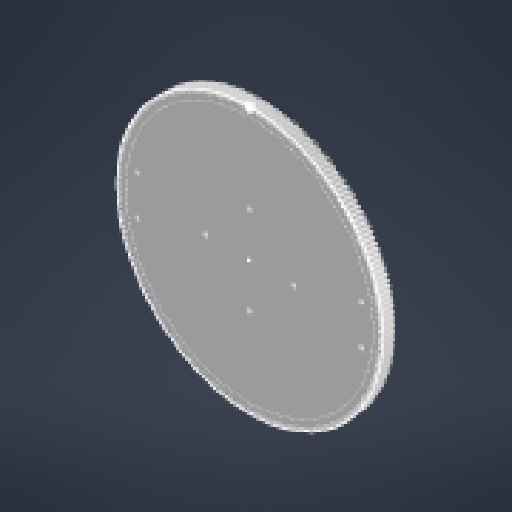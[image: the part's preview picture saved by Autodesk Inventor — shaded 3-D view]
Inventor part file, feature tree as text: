
AUTODESK INVENTOR PART (.ipt)
format: ipt  version: 2023.2 (Build 272271000, 271)  size: 873,472 bytes
history: native  units: mm
features: extrude x7, sketch x6, pattern_circular x1, other x1
ambient origin geometry x8: Origin, YZ Plane, XZ Plane, XY Plane, X Axis, Y Axis, Z Axis, Center Point
bodies: Solid1 (feature_tree)
feature tree (15):
  sketch  "Sketch1"  dims[d0=10.0mm d1=0.0mm]
  extrude  "Extrusion1"  TaperAngle=0.0deg  [1 undecoded]
  extrude  "Extrusion2"  Depth=10.0mm TaperAngle=360.0deg
  pattern_circular  "Circular Pattern1"  [2 undecoded]
  extrude  "Extrusion14"  Depth=10.0mm TaperAngle=0.0deg
  extrude  "Extrusion15"  Depth=10.0mm
  extrude  "Extrusion23"  Depth=10.0mm
  extrude  "Extrusion24"  Depth=10.0mm TaperAngle=0.0deg
  sketch  "Sketch20"  dims[d2=10.0mm d3=0.0mm d4=2000.0mm d5=360.0deg]
  sketch  "Sketch21"  dims[d80=4.0mm]
  sketch  "Sketch29"  dims[d81=4.0mm]
  sketch  "Sketch30"  dims[d82=10.0mm d83=0.0mm]
  sketch  "Sketch31"  dims[d84=4.0mm d85=4.0mm d86=10.0mm d87=0.0mm d116=4.0mm d120=4.0mm d122=10.0mm d123=0.0mm d124=4.0mm d125=4.0mm d126=10.0mm d127=10.0mm d128=10.0mm d129=10.0mm d130=10.0mm d134=10.0mm d135=10.0mm d136=10.0mm d137=10.0mm d138=10.0mm d139=0.0mm d140=0.0mm d141=10.0mm d142=0.0mm d64=1.0mm d65=1.0mm d66=1.0mm d67=0.15mm d68=0.25mm d69=0.375mm d70=14.3117mm d71=0.75mm d72=20.594885mm d73=0.0625mm d74=0.75mm d75=0.375mm]
  other  "Srf1"
  extrude  "ExtrusionSrf1"  Depth=10.0mm
note: 3 required parameter values undecoded (feature->parameter linkage not recoverable at this tier; creation-order binding heuristic only, values carry confidence <= 0.55)
